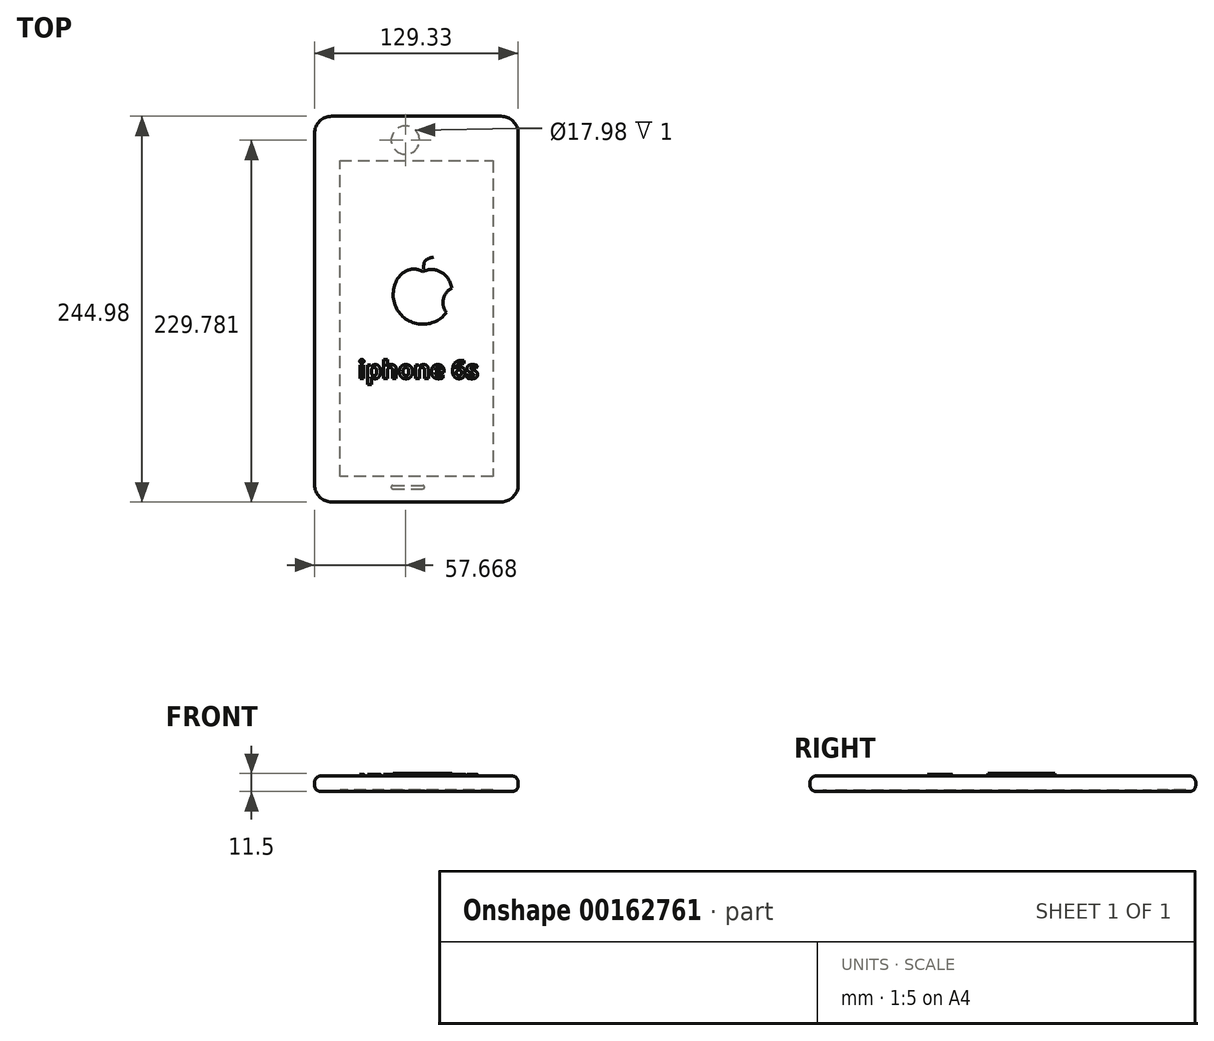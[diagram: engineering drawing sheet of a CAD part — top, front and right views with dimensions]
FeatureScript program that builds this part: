
annotation { "Feature Type Name" : "Feature", "Feature Type Description" : "" }
export const myFeature = defineFeature(function(context is Context, id is Id, definition is map)
    precondition{}
    {
        {
            var Q0;
            Q0=qCreatedBy(makeId("Top.planeOp"),FACE);
            var sketch = newSketch(context, id + "F0", { "sketchPlane" : qUnion([Q0])});
            skLineSegment(sketch, "E0.bottom", {"start": v(-68.83, 166.59) * mm, "end": v(60.5, 166.59) * mm});
            skLineSegment(sketch, "E0.top", {"start": v(-68.83, -78.39) * mm, "end": v(60.5, -78.39) * mm});
            skLineSegment(sketch, "E0.left", {"start": v(-68.83, 166.59) * mm, "end": v(-68.83, -78.39) * mm});
            skLineSegment(sketch, "E0.right", {"start": v(60.5, 166.59) * mm, "end": v(60.5, -78.39) * mm});
            skPoint(sketch, "E0.middle", {"position": v(-4.16, 44.1) * mm});
            skSolve(sketch);
        }
        {
            var Q0;
            Q0=makeQuery(id+"F0.imprint","IMPRINT",FACE,{"disambiguationData":[TD([[makeQuery(id+"F0.imprint","IMPRINT",EDGE,{"derivedFrom":sQuery(id+"F0.wireOp",EDGE,"E0.bottom")}),-1.0]])]});
            extrude(context, id + "F1", {"entities" : qUnion([Q0]), "oppositeDirection" : true, "depth" : 10 * mm});
        }
        {
            var Q0;
            Q0=makeQuery(id+"F1.opExtrude","CAP_FACE",FACE,{"disambiguationData":[OSD([sQuery(id+"F0.wireOp",EDGE,"E0.bottom"),sQuery(id+"F0.wireOp",EDGE,"E0.top"),sQuery(id+"F0.wireOp",EDGE,"E0.left"),sQuery(id+"F0.wireOp",EDGE,"E0.right")])],"isStart":false});
            var sketch = newSketch(context, id + "F2", { "sketchPlane" : qUnion([Q0])});
            skSolve(sketch);
        }
        {
            var Q0;
            Q0=makeQuery(id+"F2.imprint","IMPRINT",FACE,{"disambiguationData":[TD([[makeQuery(id+"F2.imprint","IMPRINT",EDGE,{"derivedFrom":makeQuery(id+"F1.opExtrude","CAP_EDGE",EDGE,{"disambiguationData":[OSD([sQuery(id+"F0.wireOp",EDGE,"E0.bottom")])],"isStart":false})}),1.0]])]});
            var sketch = newSketch(context, id + "F3", { "sketchPlane" : qUnion([Q0])});
            skLineSegment(sketch, "E1.0", {"start": v(-52.75, 62.3) * mm, "end": v(-52.75, -138.38) * mm});
            skLineSegment(sketch, "E1.1", {"start": v(44.43, 62.3) * mm, "end": v(-52.75, 62.3) * mm});
            skLineSegment(sketch, "E1.2", {"start": v(44.43, -138.38) * mm, "end": v(44.43, 62.3) * mm});
            skLineSegment(sketch, "E1.3", {"start": v(-52.75, -138.38) * mm, "end": v(44.43, -138.38) * mm});
            skCircle(sketch, "E2", {"center": v(-11.16, -151.4) * mm, "radius": 9 * mm});
            skLineSegment(sketch, "E3", {"start": v(-19.15, 69.01) * mm, "end": v(0, 69.01) * mm});
            skArc(sketch, "E4.0.startCap", {"start": v(-19.15, 68.01) * mm, "mid": v(-20.15, 69.01) * mm, "end": v(-19.15, 70.01) * mm});
            skArc(sketch, "E4.0.endCap", {"start": v(0, 70.01) * mm, "mid": v(1, 69.01) * mm, "end": v(0, 68.01) * mm});
            skLineSegment(sketch, "E4.0.left", {"start": v(-19.15, 70.01) * mm, "end": v(0, 70.01) * mm});
            skLineSegment(sketch, "E4.0.right", {"start": v(-19.15, 68.01) * mm, "end": v(0, 68.01) * mm});
            skSolve(sketch);
        }
        {
            var Q0;
            Q0 = qSketchRegion(id + "F3", true);
            extrude(context, id + "F4", {"entities" : qUnion([Q0]), "operationType" : NewBodyOperationType.REMOVE, "oppositeDirection" : true, "depth" : 1 * mm});
        }
        {
            var Q0;
            Q0=makeQuery(id+"F1.opExtrude","SWEPT_EDGE",EDGE,{"disambiguationData":[OSD([sQuery(id+"F0.wireOp",EDGE,"E0.top"),sQuery(id+"F0.wireOp",EDGE,"E0.left")])]});
            var Q1;
            Q1=makeQuery(id+"F1.opExtrude","SWEPT_EDGE",EDGE,{"disambiguationData":[OSD([sQuery(id+"F0.wireOp",EDGE,"E0.top"),sQuery(id+"F0.wireOp",EDGE,"E0.right")])]});
            var Q2;
            Q2=makeQuery(id+"F1.opExtrude","SWEPT_EDGE",EDGE,{"disambiguationData":[OSD([sQuery(id+"F0.wireOp",EDGE,"E0.bottom"),sQuery(id+"F0.wireOp",EDGE,"E0.right")])]});
            var Q3;
            Q3=makeQuery(id+"F1.opExtrude","SWEPT_EDGE",EDGE,{"disambiguationData":[OSD([sQuery(id+"F0.wireOp",EDGE,"E0.bottom"),sQuery(id+"F0.wireOp",EDGE,"E0.left")])]});
            fillet(context, id + "F5", {"entities" : qUnion([Q0, Q1, Q2, Q3]), "radius" : 10.86 * mm, "tangentPropagation" : true, "allowEdgeOverflow" : false});
        }
        {
            var Q0;
            Q0=makeQuery(id+"F1.opExtrude","CAP_EDGE",EDGE,{"disambiguationData":[OSD([sQuery(id+"F0.wireOp",EDGE,"E0.left")])],"isStart":true});
            var Q1;
            Q1=makeQuery(id+"F1.opExtrude","CAP_EDGE",EDGE,{"disambiguationData":[OSD([sQuery(id+"F0.wireOp",EDGE,"E0.left")])],"isStart":false});
            fillet(context, id + "F6", {"entities" : qUnion([Q0, Q1]), "radius" : 4 * mm, "tangentPropagation" : true, "allowEdgeOverflow" : false});
        }
        {
            var Q0;
            Q0=makeQuery(id+"F1.opExtrude","CAP_FACE",FACE,{"disambiguationData":[OSD([sQuery(id+"F0.wireOp",EDGE,"E0.bottom"),sQuery(id+"F0.wireOp",EDGE,"E0.top"),sQuery(id+"F0.wireOp",EDGE,"E0.left"),sQuery(id+"F0.wireOp",EDGE,"E0.right")])],"isStart":true});
            var sketch = newSketch(context, id + "F7", { "sketchPlane" : qUnion([Q0])});
            skText(sketch, "E5", { "text": "iphone 6s", "fontName": "OpenSans-Bold.ttf"});
            const initialGuessF7  = {"E5": [-0.04122, 0, 1, 0, 0.0115]};
            skSetInitialGuess(sketch, initialGuessF7);
            skSolve(sketch);
        }
        {
            var Q0;
            Q0 = qSketchRegion(id + "F7", true);
            extrude(context, id + "F8", {"entities" : qUnion([Q0]), "operationType" : NewBodyOperationType.ADD, "depth" : 1 * mm});
        }
        {
            var Q0;
            {var subQ0=sQuery(id+"F0.wireOp",EDGE,"E0.right");var subQ1=sQuery(id+"F0.wireOp",EDGE,"E0.left");var subQ2=sQuery(id+"F0.wireOp",EDGE,"E0.top");var subQ3=sQuery(id+"F0.wireOp",EDGE,"E0.bottom");var subQ4=makeQuery(id+"F1.opExtrude","CAP_FACE",FACE,{"disambiguationData":[OSD([subQ3,subQ2,subQ1,subQ0])],"isStart":true});Q0=makeQuery(id+"F8.boolean.opBoolean","SPLIT",FACE,{"disambiguationData":[TD([makeQuery(id+"F8.opExtrude","SWEPT_FACE",FACE,{"disambiguationData":[OSD([sQuery(id+"F7.wireOp",EDGE,"E5.sketch_text.stroke-0")])]})])],"derivedFrom":subQ4});}
            var sketch = newSketch(context, id + "F9", { "sketchPlane" : qUnion([Q0])});
            skCircle(sketch, "E6", {"center": v(0, 53.37) * mm, "radius": 18.9 * mm});
            skCircle(sketch, "E7", {"center": v(23.21, 48.23) * mm, "radius": 10.48 * mm});
            skFitSpline(sketch, "E8", {"points": [v(-14.46, 65.54) * mm, v(0, 67.94) * mm], "startDerivative": vector(12.03, 10.73) * mm, "endDerivative": vector(18.81, -9.77) * mm});
            skFitSpline(sketch, "E9", {"points": [v(0, 67.94) * mm, v(14.95, 64.92) * mm], "startDerivative": vector(16.7, 7.48) * mm, "endDerivative": vector(15.47, -13.82) * mm});
            skSolve(sketch);
        }
        {
            var Q0;
            {var subQ0=sQuery(id+"F9.wireOp",EDGE,"E8");Q0=makeQuery(id+"F9.imprint","IMPRINT",FACE,{"disambiguationData":[TD([[makeQuery(id+"F9.imprint","IMPRINT",EDGE,{"derivedFrom":subQ0}),-1.0]])]});}
            extrude(context, id + "F10", {"entities" : qUnion([Q0]), "operationType" : NewBodyOperationType.ADD, "depth" : 1.5 * mm});
        }
        {
            var Q0;
            {var subQ0=sQuery(id+"F0.wireOp",EDGE,"E0.right");var subQ1=sQuery(id+"F0.wireOp",EDGE,"E0.left");var subQ2=sQuery(id+"F0.wireOp",EDGE,"E0.top");var subQ3=sQuery(id+"F0.wireOp",EDGE,"E0.bottom");var subQ4=makeQuery(id+"F1.opExtrude","CAP_FACE",FACE,{"disambiguationData":[OSD([subQ3,subQ2,subQ1,subQ0])],"isStart":true});Q0=makeQuery(id+"F8.boolean.opBoolean","SPLIT",FACE,{"disambiguationData":[TD([makeQuery(id+"F8.opExtrude","SWEPT_FACE",FACE,{"disambiguationData":[OSD([sQuery(id+"F7.wireOp",EDGE,"E5.sketch_text.stroke-0")])]})])],"derivedFrom":subQ4});}
            var sketch = newSketch(context, id + "F11", { "sketchPlane" : qUnion([Q0])});
            skFitSpline(sketch, "E10", {"points": [v(0.36, 69.46) * mm, v(6.64, 77.16) * mm], "startDerivative": vector(0.27, 12.13) * mm, "endDerivative": vector(17.99, 3.3) * mm});
            skLineSegment(sketch, "E11", {"start": v(6.64, 77.16) * mm, "end": v(0.36, 69.46) * mm, "construction": true});
            skFitSpline(sketch, "E12.MirrorCS", {"points": [v(0.36, 69.46) * mm, v(6.64, 77.16) * mm], "startDerivative": vector(11.83, 2.7) * mm, "endDerivative": vector(-0.38, 18.28) * mm});
            skSolve(sketch);
        }
        {
            var Q0;
            Q0=makeQuery(id+"F11.imprint","IMPRINT",FACE,{"disambiguationData":[TD([[makeQuery(id+"F11.imprint","IMPRINT",EDGE,{"derivedFrom":sQuery(id+"F11.wireOp",EDGE,"E10")}),-1.0]])]});
            var Q1;
            Q1=makeQuery(id+"F10.opExtrude","CAP_FACE",FACE,{"disambiguationData":[OSD([sQuery(id+"F9.wireOp",EDGE,"E6"),sQuery(id+"F9.wireOp",EDGE,"E7"),sQuery(id+"F9.wireOp",EDGE,"E8"),sQuery(id+"F9.wireOp",EDGE,"E9")])],"isStart":false});
            extrude(context, id + "F12", {"entities" : qUnion([Q0]), "operationType" : NewBodyOperationType.ADD, "endBound" : BoundingType.UP_TO_SURFACE, "endBoundEntityFace" : qUnion([Q1]), "depth" : 6.25 * mm});
        }
    });
